# Revit family: 712-1020-001-DN40-300
name_source: partatom
category: Pipe Accessories
units: mm (PartAtom-declared; Revit-internal decimal feet)

## family parameters
Always vertical = Yes
Cut with Voids When Loaded = No
Part Type = Valve - Breaks Into
Round Connector Dimension = Use Diameter
Shared = No
Work Plane-Based = No

## types (69) — shared parameters
712-0040-10-201 = DN40_PN10/16
712-0050-10-201 = DN50_PN10/16
712-0051-10-201 = DN50_PN10/16
712-0065-10-201 = DN65_PN10/16
712-0066-10-201 = DN65_PN10/16
712-0067-10-201 = DN65_PN10/16
712-0080-10-201 = DN80_PN10/16
712-0081-10-201 = DN80_PN10/16
712-0082-10-201 = DN80_PN10/16
712-0083-10-201 = DN80_PN10/16
712-0100-10-201 = DN100_PN10/16
712-0101-10-201 = DN100_PN10/16
712-0102-10-201 = DN100_PN10/16
712-0103-10-201 = DN100_PN10/16
712-0104-10-201 = DN100_PN10/16
712-0125-10-201 = DN125_PN10/16
712-0126-10-201 = DN125_PN10/16
712-0127-10-201 = DN125_PN10/16
712-0128-10-201 = DN125_PN10/16
712-0129-10-201 = DN125_PN10/16
712-0130-10-201 = DN125_PN10/16
712-0150-10-201 = DN150_PN10/16
712-0151-10-201 = DN150_PN10/16
712-0152-10-201 = DN150_PN10/16
712-0153-10-201 = DN150_PN10/16
712-0154-10-201 = DN150_PN10/16
712-0155-10-201 = DN150_PN10/16
712-0156-10-201 = DN150_PN10/16
712-0200-10-200 = DN200_PN10/16
712-0200-10-201 = DN200_PN10/16
712-0201-10-200 = DN200_PN10/16
712-0201-10-201 = DN200_PN10/16
712-0202-10-200 = DN200_PN10/16
712-0202-10-201 = DN200_PN10/16
712-0203-10-200 = DN200_PN10/16
712-0203-10-201 = DN200_PN10/16
712-0204-10-200 = DN200_PN10/16
712-0204-10-201 = DN200_PN10/16
712-0205-10-200 = DN200_PN10/16
712-0205-10-201 = DN200_PN10/16
712-0206-10-200 = DN200_PN10/16
712-0206-10-201 = DN200_PN10/16
712-0207-10-200 = DN200_PN10/16
712-0250-10-200 = DN250_PN10/16
712-0250-10-201 = DN250_PN10/16
712-0251-10-200 = DN250_PN10/16
712-0251-10-201 = DN250_PN10/16
712-0252-10-200 = DN250_PN10/16
712-0252-10-201 = DN250_PN10/16
712-0253-10-200 = DN250_PN10/16
712-0253-10-201 = DN250_PN10/16
712-0254-10-200 = DN250_PN10/16
712-0254-10-201 = DN250_PN10/16
712-0255-10-200 = DN250_PN10/16
712-0255-10-201 = DN250_PN10/16
712-0256-10-200 = DN250_PN10/16
712-0256-10-201 = DN250_PN10/16
712-0300-10-200 = DN300_PN10/16
712-0300-10-201 = DN300_PN10/16
712-0301-10-200 = DN300_PN10/16
712-0301-10-201 = DN300_PN10/16
712-0302-10-200 = DN300_PN10/16
712-0302-10-201 = DN300_PN10/16
712-0303-10-200 = DN300_PN10/16
712-0303-10-201 = DN300_PN10/16
712-0305-10-200 = DN300_PN10/16
712-0305-10-201 = DN300_PN10/16
712-0306-10-200 = DN300_PN10/16
712-0306-10-201 = DN300_PN10/16
Body_wallthickness = 10 mm  [stored 0.0328084 ft]
RF_Thick = 3 mm  [stored 0.00984252 ft]
Search_Table = 712-1020-001-DN40-300
URL product pages = https://www.avkvalves.com

## per-type parameters (varying)
| type | Ch | DN2 | Description_ | FOD | Flange_thickness | H | Hook | Hook_2 | ID | ID2 | L | Nominal Diameter (DN) | Rf_Dia | Rib |
| 712-0040-10-201_DN40_PN10/16 | 31 mm  [stored 0.101706 ft] | 40 mm  [stored 0.131234 ft] | AVK FLANGED TEE W/LOOSE FLANGES | 75 mm | 19 mm  [stored 0.062336 ft] | 140 mm | 50 mm  [stored 0.164042 ft] | 50 mm  [stored 0.164042 ft] | 20 mm  [stored 0.0656168 ft] | 20 mm  [stored 0.0656168 ft] | 280 mm | 40 mm  [stored 0.131234 ft] | 42 mm  [stored 0.137795 ft] | 10 mm  [stored 0.0328084 ft] |
| 712-0050-10-201_DN50_PN10/16 | 37.25 mm  [stored 0.122211 ft] | 50 mm  [stored 0.164042 ft] | AVK FLANGED TEE W/LOOSE FLANGES | 82.5 mm | 19 mm  [stored 0.062336 ft] | 150 mm | 55 mm  [stored 0.180446 ft] | 55 mm  [stored 0.180446 ft] | 25 mm  [stored 0.082021 ft] | 25 mm  [stored 0.082021 ft] | 300 mm | 50 mm  [stored 0.164042 ft] | 49.5 mm  [stored 0.162402 ft] | 10 mm  [stored 0.0328084 ft] |
| 712-0051-10-201_DN50_PN10/16 | 37.28 mm | 40 mm  [stored 0.131234 ft] | AVK FLANGED TEE W/LOOSE FLANGES | 82.5 mm | 19 mm  [stored 0.062336 ft] | 140 mm | 55.05 mm | 50 mm  [stored 0.164042 ft] | 25.05 mm | 20 mm  [stored 0.0656168 ft] | 300 mm | 50.1 mm  [stored 0.16437 ft] | 49.5 mm  [stored 0.162402 ft] | 10 mm  [stored 0.0328084 ft] |
| 712-0065-10-201_DN65_PN10/16 | 45.75 mm | 65 mm | AVK FLANGED TEE W/LOOSE FLANGES | 92.5 mm | 19 mm  [stored 0.062336 ft] | 160 mm | 62.5 mm  [stored 0.205052 ft] | 62.5 mm  [stored 0.205052 ft] | 32.5 mm  [stored 0.106627 ft] | 32.5 mm  [stored 0.106627 ft] | 320 mm | 65 mm | 59 mm | 10 mm  [stored 0.0328084 ft] |
| 712-0066-10-201_DN65_PN10/16 | 45.78 mm | 50 mm  [stored 0.164042 ft] | AVK FLANGED TEE W/LOOSE FLANGES | 92.5 mm | 19 mm  [stored 0.062336 ft] | 150 mm | 62.55 mm  [stored 0.205217 ft] | 55 mm  [stored 0.180446 ft] | 32.55 mm  [stored 0.106791 ft] | 25 mm  [stored 0.082021 ft] | 330 mm | 65.1 mm | 59 mm | 10 mm  [stored 0.0328084 ft] |
| 712-0067-10-201_DN65_PN10/16 | 45.8 mm | 40 mm  [stored 0.131234 ft] | AVK FLANGED TEE W/LOOSE FLANGES | 92.5 mm | 19 mm  [stored 0.062336 ft] | 130 mm | 62.6 mm  [stored 0.205381 ft] | 50 mm  [stored 0.164042 ft] | 32.6 mm | 20 mm  [stored 0.0656168 ft] | 300 mm | 65.2 mm | 59 mm | 10 mm  [stored 0.0328084 ft] |
| 712-0080-10-201_DN80_PN10/16 | 53 mm  [stored 0.173885 ft] | 80 mm | AVK FLANGED TEE W/LOOSE FLANGES | 100 mm | 19 mm  [stored 0.062336 ft] | 165 mm | 70 mm | 70 mm | 40 mm  [stored 0.131234 ft] | 40 mm  [stored 0.131234 ft] | 330 mm | 80 mm | 66 mm | 10 mm  [stored 0.0328084 ft] |
| 712-0081-10-201_DN80_PN10/16 | 53.03 mm | 65 mm | AVK FLANGED TEE W/LOOSE FLANGES | 100 mm | 19 mm  [stored 0.062336 ft] | 155 mm | 70.05 mm | 62.5 mm  [stored 0.205052 ft] | 40.05 mm  [stored 0.131398 ft] | 32.5 mm  [stored 0.106627 ft] | 310 mm | 80.1 mm | 66 mm | 10 mm  [stored 0.0328084 ft] |
| 712-0082-10-201_DN80_PN10/16 | 53.05 mm | 50 mm  [stored 0.164042 ft] | AVK FLANGED TEE W/LOOSE FLANGES | 100 mm | 19 mm  [stored 0.062336 ft] | 165 mm | 70.1 mm | 55 mm  [stored 0.180446 ft] | 40.1 mm  [stored 0.131562 ft] | 25 mm  [stored 0.082021 ft] | 330 mm | 80.2 mm | 66 mm | 10 mm  [stored 0.0328084 ft] |
| 712-0083-10-201_DN80_PN10/16 | 53.08 mm | 40 mm  [stored 0.131234 ft] | AVK FLANGED TEE W/LOOSE FLANGES | 100 mm | 19 mm  [stored 0.062336 ft] | 140 mm | 70.15 mm | 50 mm  [stored 0.164042 ft] | 40.15 mm  [stored 0.131726 ft] | 20 mm  [stored 0.0656168 ft] | 310 mm | 80.3 mm | 66 mm | 10 mm  [stored 0.0328084 ft] |
| 712-0100-10-201_DN100_PN10/16 | 64 mm | 100 mm | AVK FLANGED TEE W/LOOSE FLANGES | 110 mm | 19 mm  [stored 0.062336 ft] | 180 mm | 80 mm | 80 mm | 50 mm  [stored 0.164042 ft] | 50 mm  [stored 0.164042 ft] | 360 mm | 100 mm | 78 mm | 10 mm  [stored 0.0328084 ft] |
| 712-0101-10-201_DN100_PN10/16 | 64.03 mm | 80 mm | AVK FLANGED TEE W/LOOSE FLANGES | 110 mm | 19 mm  [stored 0.062336 ft] | 175 mm | 80.05 mm | 70 mm | 50.05 mm  [stored 0.164206 ft] | 40 mm  [stored 0.131234 ft] | 360 mm | 100.1 mm | 78 mm | 10 mm  [stored 0.0328084 ft] |
| 712-0102-10-201_DN100_PN10/16 | 64.05 mm | 65 mm | AVK FLANGED TEE W/LOOSE FLANGES | 110 mm | 19 mm  [stored 0.062336 ft] | 165 mm | 80.1 mm | 62.5 mm  [stored 0.205052 ft] | 50.1 mm  [stored 0.16437 ft] | 32.5 mm  [stored 0.106627 ft] | 320 mm | 100.2 mm | 78 mm | 10 mm  [stored 0.0328084 ft] |
| 712-0103-10-201_DN100_PN10/16 | 64.08 mm | 50 mm  [stored 0.164042 ft] | AVK FLANGED TEE W/LOOSE FLANGES | 110 mm | 19 mm  [stored 0.062336 ft] | 160 mm | 80.15 mm | 55 mm  [stored 0.180446 ft] | 50.15 mm | 25 mm  [stored 0.082021 ft] | 360 mm | 100.3 mm | 78 mm | 10 mm  [stored 0.0328084 ft] |
| 712-0104-10-201_DN100_PN10/16 | 64.1 mm | 40 mm  [stored 0.131234 ft] | AVK FLANGED TEE W/LOOSE FLANGES | 110 mm | 19 mm  [stored 0.062336 ft] | 145 mm | 80.2 mm | 50 mm  [stored 0.164042 ft] | 50.2 mm  [stored 0.164698 ft] | 20 mm  [stored 0.0656168 ft] | 320 mm | 100.4 mm | 78 mm | 10 mm  [stored 0.0328084 ft] |
| 712-0125-10-201_DN125_PN10/16 | 77.25 mm | 125 mm | AVK CROSS Loose flange | 125 mm | 19 mm  [stored 0.062336 ft] | 200 mm | 92.5 mm | 92.5 mm | 62.5 mm  [stored 0.205052 ft] | 62.5 mm  [stored 0.205052 ft] | 400 mm | 125 mm | 92 mm | 15 mm  [stored 0.0492126 ft] |
| 712-0126-10-201_DN125_PN10/16 | 77.28 mm | 100 mm | AVK FLANGED TEE W/LOOSE FLANGES | 125 mm | 19 mm  [stored 0.062336 ft] | 195 mm | 92.55 mm | 80 mm | 62.55 mm  [stored 0.205217 ft] | 50 mm  [stored 0.164042 ft] | 400 mm | 125.1 mm | 92 mm | 15 mm  [stored 0.0492126 ft] |
| 712-0127-10-201_DN125_PN10/16 | 77.3 mm | 80 mm | AVK FLANGED TEE W/LOOSE FLANGES | 125 mm | 19 mm  [stored 0.062336 ft] | 190 mm | 92.6 mm | 70 mm | 62.6 mm  [stored 0.205381 ft] | 40 mm  [stored 0.131234 ft] | 400 mm | 125.2 mm | 92 mm | 15 mm  [stored 0.0492126 ft] |
| 712-0128-10-201_DN125_PN10/16 | 77.33 mm | 65 mm | AVK FLANGED TEE W/LOOSE FLANGES | 125 mm | 19 mm  [stored 0.062336 ft] | 180 mm | 92.65 mm | 62.5 mm  [stored 0.205052 ft] | 62.65 mm | 32.5 mm  [stored 0.106627 ft] | 330 mm | 125.3 mm | 92 mm | 15 mm  [stored 0.0492126 ft] |
| 712-0129-10-201_DN125_PN10/16 | 77.35 mm | 50 mm  [stored 0.164042 ft] | AVK FLANGED TEE W/LOOSE FLANGES | 125 mm | 19 mm  [stored 0.062336 ft] | 175 mm | 92.7 mm | 55 mm  [stored 0.180446 ft] | 62.7 mm | 25 mm  [stored 0.082021 ft] | 400 mm | 125.4 mm | 92 mm | 15 mm  [stored 0.0492126 ft] |
| 712-0130-10-201_DN125_PN10/16 | 77.38 mm | 40 mm  [stored 0.131234 ft] | AVK FLANGED TEE W/LOOSE FLANGES | 125 mm | 19 mm  [stored 0.062336 ft] | 160 mm | 92.75 mm | 50 mm  [stored 0.164042 ft] | 62.75 mm | 20 mm  [stored 0.0656168 ft] | 330 mm | 125.5 mm | 92 mm | 15 mm  [stored 0.0492126 ft] |
| 712-0150-10-201_DN150_PN10/16 | 90.25 mm | 150 mm | AVK FLANGED TEE W/LOOSE FLANGES | 142.5 mm | 20 mm  [stored 0.0656168 ft] | 220 mm | 105 mm | 105 mm | 75 mm | 75 mm | 440 mm | 150 mm | 105.5 mm | 20 mm  [stored 0.0656168 ft] |
| 712-0151-10-201_DN150_PN10/16 | 90.28 mm | 125 mm | AVK FLANGED TEE W/LOOSE FLANGES | 142.5 mm | 20 mm  [stored 0.0656168 ft] | 215 mm | 105.05 mm | 92.5 mm | 75.05 mm | 62.5 mm  [stored 0.205052 ft] | 440 mm | 150.1 mm | 105.5 mm | 20 mm  [stored 0.0656168 ft] |
| 712-0152-10-201_DN150_PN10/16 | 90.3 mm | 100 mm | AVK FLANGED TEE W/LOOSE FLANGES | 142.5 mm | 20 mm  [stored 0.0656168 ft] | 210 mm | 105.1 mm | 80 mm | 75.1 mm | 50 mm  [stored 0.164042 ft] | 440 mm | 150.2 mm | 105.5 mm | 20 mm  [stored 0.0656168 ft] |
| 712-0153-10-201_DN150_PN10/16 | 90.33 mm | 80 mm | AVK FLANGED TEE W/LOOSE FLANGES | 142.5 mm | 20 mm  [stored 0.0656168 ft] | 205 mm | 105.15 mm | 70 mm | 75.15 mm | 40 mm  [stored 0.131234 ft] | 440 mm | 150.3 mm | 105.5 mm | 20 mm  [stored 0.0656168 ft] |
| 712-0154-10-201_DN150_PN10/16 | 90.35 mm | 65 mm | AVK FLANGED TEE W/LOOSE FLANGES | 142.5 mm | 20 mm  [stored 0.0656168 ft] | 190 mm | 105.2 mm | 62.5 mm  [stored 0.205052 ft] | 75.2 mm | 32.5 mm  [stored 0.106627 ft] | 440 mm | 150.4 mm | 105.5 mm | 20 mm  [stored 0.0656168 ft] |
| 712-0155-10-201_DN150_PN10/16 | 90.38 mm | 50 mm  [stored 0.164042 ft] | AVK FLANGED TEE W/LOOSE FLANGES | 142.5 mm | 20 mm  [stored 0.0656168 ft] | 185 mm | 105.25 mm | 55 mm  [stored 0.180446 ft] | 75.25 mm | 25 mm  [stored 0.082021 ft] | 440 mm | 150.5 mm | 105.5 mm | 20 mm  [stored 0.0656168 ft] |
| 712-0156-10-201_DN150_PN10/16 | 90.4 mm | 40 mm  [stored 0.131234 ft] | AVK FLANGED TEE W/LOOSE FLANGES | 142.5 mm | 20 mm  [stored 0.0656168 ft] | 190 mm | 105.3 mm | 50 mm  [stored 0.164042 ft] | 75.3 mm | 20 mm  [stored 0.0656168 ft] | 440 mm | 150.6 mm | 105.5 mm | 20 mm  [stored 0.0656168 ft] |
| 712-0200-10-200_DN200_PN10/16 | 116.5 mm | 200 mm | AVK FLANGED TEE W/LOOSE FLANGES | 170 mm | 20 mm  [stored 0.0656168 ft] | 260 mm | 130 mm | 130 mm | 100 mm | 100 mm | 520 mm | 200 mm | 133 mm | 25 mm  [stored 0.082021 ft] |
| 712-0200-10-201_DN200_PN10/16 | 116.53 mm | 200 mm | AVK FLANGED TEE W/LOOSE FLANGES | 170 mm | 20 mm  [stored 0.0656168 ft] | 260 mm | 130.05 mm | 130 mm | 100.05 mm | 100 mm | 520 mm | 200.1 mm | 133 mm | 25 mm  [stored 0.082021 ft] |
| 712-0201-10-200_DN200_PN10/16 | 116.55 mm | 150 mm | AVK FLANGED TEE W/LOOSE FLANGES | 170 mm | 20 mm  [stored 0.0656168 ft] | 250 mm | 130.1 mm | 105 mm | 100.1 mm | 75 mm | 520 mm | 200.2 mm | 133 mm | 25 mm  [stored 0.082021 ft] |
| 712-0201-10-201_DN200_PN10/16 | 116.58 mm | 150 mm | AVK FLANGED TEE W/LOOSE FLANGES | 170 mm | 20 mm  [stored 0.0656168 ft] | 250 mm | 130.15 mm | 105 mm | 100.15 mm | 75 mm | 520 mm | 200.3 mm | 133 mm | 25 mm  [stored 0.082021 ft] |
| 712-0202-10-200_DN200_PN10/16 | 116.6 mm | 125 mm | AVK FLANGED TEE W/LOOSE FLANGES
AVK FLANGED TEE W/LOOSE FLANGES | 170 mm | 20 mm  [stored 0.0656168 ft] | 240 mm | 130.2 mm | 92.5 mm | 100.2 mm | 62.5 mm  [stored 0.205052 ft] | 435 mm | 200.4 mm | 133 mm | 25 mm  [stored 0.082021 ft] |
| 712-0202-10-201_DN200_PN10/16 | 116.63 mm | 125 mm | AVK FLANGED TEE W/LOOSE FLANGES | 170 mm | 20 mm  [stored 0.0656168 ft] | 240 mm | 130.25 mm | 92.5 mm | 100.25 mm | 62.5 mm  [stored 0.205052 ft] | 435 mm | 200.5 mm | 133 mm | 25 mm  [stored 0.082021 ft] |
| 712-0203-10-200_DN200_PN10/16 | 116.65 mm | 100 mm | AVK FLANGED TEE W/LOOSE FLANGES | 170 mm | 20 mm  [stored 0.0656168 ft] | 240 mm | 130.3 mm | 80 mm | 100.3 mm | 50 mm  [stored 0.164042 ft] | 520 mm | 200.6 mm | 133 mm | 25 mm  [stored 0.082021 ft] |
| 712-0203-10-201_DN200_PN10/16 | 116.68 mm | 100 mm | AVK FLANGED TEE W/LOOSE FLANGES | 170 mm | 20 mm  [stored 0.0656168 ft] | 240 mm | 130.35 mm | 80 mm | 100.35 mm | 50 mm  [stored 0.164042 ft] | 520 mm | 200.7 mm | 133 mm | 25 mm  [stored 0.082021 ft] |
| 712-0204-10-200_DN200_PN10/16 | 116.7 mm | 80 mm | AVK FLANGED TEE W/LOOSE FLANGES | 170 mm | 20 mm  [stored 0.0656168 ft] | 235 mm | 130.4 mm | 70 mm | 100.4 mm | 40 mm  [stored 0.131234 ft] | 520 mm | 200.8 mm | 133 mm | 25 mm  [stored 0.082021 ft] |
| 712-0204-10-201_DN200_PN10/16 | 116.73 mm | 80 mm | AVK FLANGED TEE W/LOOSE FLANGES | 170 mm | 20 mm  [stored 0.0656168 ft] | 235 mm | 130.45 mm | 70 mm | 100.45 mm | 40 mm  [stored 0.131234 ft] | 520 mm | 200.9 mm | 133 mm | 25 mm  [stored 0.082021 ft] |
| 712-0205-10-200_DN200_PN10/16 | 116.53 mm | 65 mm | AVK FLANGED TEE W/LOOSE FLANGES | 170 mm | 20 mm  [stored 0.0656168 ft] | 215 mm | 130.06 mm | 62.5 mm  [stored 0.205052 ft] | 100.06 mm | 32.5 mm  [stored 0.106627 ft] | 365 mm | 200.11 mm | 133 mm | 25 mm  [stored 0.082021 ft] |
| 712-0205-10-201_DN200_PN10/16 | 116.53 mm | 65 mm | AVK FLANGED TEE W/LOOSE FLANGES | 170 mm | 20 mm  [stored 0.0656168 ft] | 215 mm | 130.06 mm | 62.5 mm  [stored 0.205052 ft] | 100.06 mm | 32.5 mm  [stored 0.106627 ft] | 365 mm | 200.12 mm | 133 mm | 25 mm  [stored 0.082021 ft] |
| 712-0206-10-200_DN200_PN10/16 | 116.53 mm | 50 mm  [stored 0.164042 ft] | AVK FLANGED TEE W/LOOSE FLANGES | 170 mm | 20 mm  [stored 0.0656168 ft] | 220 mm | 130.07 mm | 55 mm  [stored 0.180446 ft] | 100.07 mm | 25 mm  [stored 0.082021 ft] | 520 mm | 200.13 mm | 133 mm | 25 mm  [stored 0.082021 ft] |
| 712-0206-10-201_DN200_PN10/16 | 116.54 mm | 50 mm  [stored 0.164042 ft] | AVK FLANGED TEE W/LOOSE FLANGES | 170 mm | 20 mm  [stored 0.0656168 ft] | 220 mm | 130.07 mm | 55 mm  [stored 0.180446 ft] | 100.07 mm | 25 mm  [stored 0.082021 ft] | 520 mm | 200.14 mm | 133 mm | 25 mm  [stored 0.082021 ft] |
| 712-0207-10-200_DN200_PN10/16 | 116.54 mm | 40 mm  [stored 0.131234 ft] | AVK FLANGED TEE W/LOOSE FLANGES | 170 mm | 20 mm  [stored 0.0656168 ft] | 195 mm | 130.08 mm | 50 mm  [stored 0.164042 ft] | 100.08 mm | 20 mm  [stored 0.0656168 ft] | 365 mm | 200.15 mm | 133 mm | 25 mm  [stored 0.082021 ft] |
| 712-0250-10-200_DN250_PN10/16 | 142.28 mm | 250 mm | AVK FLANGED TEE W/LOOSE FLANGES | 200 mm | 22 mm  [stored 0.0721785 ft] | 350 mm | 155.05 mm | 155 mm | 125.05 mm | 125 mm | 700 mm | 250.1 mm | 159.5 mm | 30 mm  [stored 0.0984252 ft] |
| 712-0250-10-201_DN250_PN10/16 | 142.3 mm | 250 mm | AVK FLANGED TEE W/LOOSE FLANGES | 200 mm | 22 mm  [stored 0.0721785 ft] | 350 mm | 155.1 mm | 155 mm | 125.1 mm | 125 mm | 700 mm | 250.2 mm | 159.5 mm | 30 mm  [stored 0.0984252 ft] |
| 712-0251-10-200_DN250_PN10/16 | 142.33 mm | 200 mm | AVK FLANGED TEE W/LOOSE FLANGES | 200 mm | 22 mm  [stored 0.0721785 ft] | 325 mm | 155.15 mm | 130 mm | 125.15 mm | 100 mm | 700 mm | 250.3 mm | 159.5 mm | 30 mm  [stored 0.0984252 ft] |
| 712-0251-10-201_DN250_PN10/16 | 142.35 mm | 200 mm | AVK FLANGED TEE W/LOOSE FLANGES | 200 mm | 22 mm  [stored 0.0721785 ft] | 325 mm | 155.2 mm | 130 mm | 125.2 mm | 100 mm | 700 mm | 250.4 mm | 159.5 mm | 30 mm  [stored 0.0984252 ft] |
| 712-0252-10-200_DN250_PN10/16 | 142.38 mm | 150 mm | AVK FLANGED TEE W/LOOSE FLANGES | 200 mm | 22 mm  [stored 0.0721785 ft] | 280 mm | 155.25 mm | 105 mm | 125.25 mm | 75 mm | 485 mm | 250.5 mm | 159.5 mm | 30 mm  [stored 0.0984252 ft] |
| 712-0252-10-201_DN250_PN10/16 | 142.4 mm | 150 mm | AVK FLANGED TEE W/LOOSE FLANGES | 200 mm | 22 mm  [stored 0.0721785 ft] | 280 mm | 155.3 mm | 105 mm | 125.3 mm | 75 mm | 485 mm | 250.6 mm | 159.5 mm | 30 mm  [stored 0.0984252 ft] |
| 712-0253-10-200_DN250_PN10/16 | 142.43 mm | 125 mm | AVK FLANGED TEE W/LOOSE FLANGES | 200 mm | 22 mm  [stored 0.0721785 ft] | 275 mm | 155.35 mm | 92.5 mm | 125.35 mm | 62.5 mm  [stored 0.205052 ft] | 460 mm | 250.7 mm | 159.5 mm | 30 mm  [stored 0.0984252 ft] |
| 712-0253-10-201_DN250_PN10/16 | 142.45 mm | 125 mm | AVK FLANGED TEE W/LOOSE FLANGES | 200 mm | 22 mm  [stored 0.0721785 ft] | 275 mm | 155.4 mm | 92.5 mm | 125.4 mm | 62.5 mm  [stored 0.205052 ft] | 460 mm | 250.8 mm | 159.5 mm | 30 mm  [stored 0.0984252 ft] |
| 712-0254-10-200_DN250_PN10/16 | 142.48 mm | 100 mm | AVK FLANGED TEE W/LOOSE FLANGES | 200 mm | 22 mm  [stored 0.0721785 ft] | 275 mm | 155.45 mm | 80 mm | 125.45 mm | 50 mm  [stored 0.164042 ft] | 700 mm | 250.9 mm | 159.5 mm | 30 mm  [stored 0.0984252 ft] |
| 712-0254-10-201_DN250_PN10/16 | 142.28 mm | 100 mm | AVK FLANGED TEE W/LOOSE FLANGES | 200 mm | 22 mm  [stored 0.0721785 ft] | 275 mm | 155.06 mm | 80 mm | 125.06 mm | 50 mm  [stored 0.164042 ft] | 700 mm | 250.11 mm | 159.5 mm | 30 mm  [stored 0.0984252 ft] |
| 712-0255-10-200_DN250_PN10/16 | 142.28 mm | 80 mm | AVK FLANGED TEE W/LOOSE FLANGES | 200 mm | 22 mm  [stored 0.0721785 ft] | 265 mm | 155.06 mm | 70 mm | 125.06 mm | 40 mm  [stored 0.131234 ft] | 405 mm | 250.12 mm | 159.5 mm | 30 mm  [stored 0.0984252 ft] |
| 712-0255-10-201_DN250_PN10/16 | 142.28 mm | 80 mm | AVK FLANGED TEE W/LOOSE FLANGES | 200 mm | 22 mm  [stored 0.0721785 ft] | 265 mm | 155.07 mm | 70 mm | 125.07 mm | 40 mm  [stored 0.131234 ft] | 405 mm | 250.13 mm | 159.5 mm | 30 mm  [stored 0.0984252 ft] |
| 712-0256-10-200_DN250_PN10/16 | 142.29 mm | 65 mm | AVK FLANGED TEE W/LOOSE FLANGES | 200 mm | 22 mm  [stored 0.0721785 ft] | 260 mm | 155.07 mm | 62.5 mm  [stored 0.205052 ft] | 125.07 mm | 32.5 mm  [stored 0.106627 ft] | 385 mm | 250.14 mm | 159.5 mm | 30 mm  [stored 0.0984252 ft] |
| 712-0256-10-201_DN250_PN10/16 | 142.29 mm | 65 mm | AVK FLANGED TEE W/LOOSE FLANGES | 200 mm | 22 mm  [stored 0.0721785 ft] | 260 mm | 155.08 mm | 62.5 mm  [stored 0.205052 ft] | 125.08 mm | 32.5 mm  [stored 0.106627 ft] | 385 mm | 250.15 mm | 159.5 mm | 30 mm  [stored 0.0984252 ft] |
| 712-0300-10-200_DN300_PN10/16 | 167.53 mm | 300 mm | AVK FLANGED TEE W/LOOSE FLANGES | 227.5 mm | 24 mm  [stored 0.0787402 ft] | 400 mm | 180.05 mm | 180 mm | 150.05 mm | 150 mm | 800 mm | 300.1 mm | 185 mm | 30 mm  [stored 0.0984252 ft] |
| 712-0300-10-201_DN300_PN10/16 | 167.55 mm | 300 mm | AVK FLANGED TEE W/LOOSE FLANGES | 227.5 mm | 24 mm  [stored 0.0787402 ft] | 400 mm | 180.1 mm | 180 mm | 150.1 mm | 150 mm | 800 mm | 300.2 mm | 185 mm | 30 mm  [stored 0.0984252 ft] |
| 712-0301-10-200_DN300_PN10/16 | 167.58 mm | 250 mm | AVK FLANGED TEE W/LOOSE FLANGES | 227.5 mm | 24 mm  [stored 0.0787402 ft] | 330 mm | 180.15 mm | 155 mm | 150.15 mm | 125 mm | 620 mm | 300.3 mm | 185 mm | 30 mm  [stored 0.0984252 ft] |
| 712-0301-10-201_DN300_PN10/16 | 167.6 mm | 250 mm | AVK FLANGED TEE W/LOOSE FLANGES | 227.5 mm | 24 mm  [stored 0.0787402 ft] | 330 mm | 180.2 mm | 155 mm | 150.2 mm | 125 mm | 620 mm | 300.4 mm | 185 mm | 30 mm  [stored 0.0984252 ft] |
| 712-0302-10-200_DN300_PN10/16 | 167.63 mm | 200 mm | AVK FLANGED TEE W/LOOSE FLANGES | 227.5 mm | 24 mm  [stored 0.0787402 ft] | 350 mm | 180.25 mm | 130 mm | 150.25 mm | 100 mm | 800 mm | 300.5 mm | 185 mm | 30 mm  [stored 0.0984252 ft] |
| 712-0302-10-201_DN300_PN10/16 | 167.65 mm | 200 mm | AVK FLANGED TEE W/LOOSE FLANGES | 227.5 mm | 24 mm  [stored 0.0787402 ft] | 350 mm | 180.3 mm | 130 mm | 150.3 mm | 100 mm | 800 mm | 300.6 mm | 185 mm | 30 mm  [stored 0.0984252 ft] |
| 712-0303-10-200_DN300_PN10/16 | 167.68 mm | 150 mm | AVK FLANGED TEE W/LOOSE FLANGES | 227.5 mm | 24 mm  [stored 0.0787402 ft] | 300 mm | 180.35 mm | 105 mm | 150.35 mm | 75 mm | 505 mm | 300.7 mm | 185 mm | 30 mm  [stored 0.0984252 ft] |
| 712-0303-10-201_DN300_PN10/16 | 167.7 mm | 150 mm | AVK FLANGED TEE W/LOOSE FLANGES | 227.5 mm | 24 mm  [stored 0.0787402 ft] | 300 mm | 180.4 mm | 105 mm | 150.4 mm | 75 mm | 505 mm | 300.8 mm | 185 mm | 30 mm  [stored 0.0984252 ft] |
| 712-0305-10-200_DN300_PN10/16 | 167.73 mm | 100 mm | AVK FLANGED TEE W/LOOSE FLANGES | 227.5 mm | 24 mm  [stored 0.0787402 ft] | 300 mm | 180.45 mm | 80 mm | 150.45 mm | 50 mm  [stored 0.164042 ft] | 800 mm | 300.9 mm | 185 mm | 30 mm  [stored 0.0984252 ft] |
| 712-0305-10-201_DN300_PN10/16 | 167.53 mm | 100 mm | AVK FLANGED TEE W/LOOSE FLANGES | 227.5 mm | 24 mm  [stored 0.0787402 ft] | 300 mm | 180.06 mm | 80 mm | 150.06 mm | 50 mm  [stored 0.164042 ft] | 800 mm | 300.11 mm | 185 mm | 30 mm  [stored 0.0984252 ft] |
| 712-0306-10-200_DN300_PN10/16 | 167.53 mm | 80 mm | AVK FLANGED TEE W/LOOSE FLANGES | 227.5 mm | 24 mm  [stored 0.0787402 ft] | 295 mm | 180.06 mm | 70 mm | 150.06 mm | 40 mm  [stored 0.131234 ft] | 425 mm | 300.12 mm | 185 mm | 30 mm  [stored 0.0984252 ft] |
| 712-0306-10-201_DN300_PN10/16 | 167.53 mm | 80 mm | AVK FLANGED TEE W/LOOSE FLANGES | 227.5 mm | 24 mm  [stored 0.0787402 ft] | 295 mm | 180.07 mm | 70 mm | 150.07 mm | 40 mm  [stored 0.131234 ft] | 425 mm | 300.13 mm | 185 mm | 30 mm  [stored 0.0984252 ft] |

note: [stored X ft] marks values corroborated as IEEE doubles in the binary element streams (Revit-internal decimal feet)

## geometry (parser evidence)
native form markers: Sweep x15
no freeform markers — native parametric forms only
